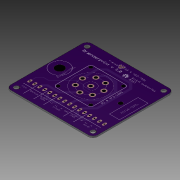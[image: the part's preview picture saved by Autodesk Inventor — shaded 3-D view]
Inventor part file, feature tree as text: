
AUTODESK INVENTOR PART (.ipt)
format: ipt  version: 2015 (Build 190159000, 159)  size: 491,008 bytes
history: native  units: mm
features: other x4, sketch x3, extrude x1
ambient origin geometry x8: Origin, YZ Plane, XZ Plane, XY Plane, X Axis, Y Axis, Z Axis, Center Point
bodies: Solid1 (feature_tree)
feature tree (8):
  extrude  "Extrusion1"  Depth=82.54mm
  other  "Decal1"
  other  "Decal2"
  sketch  "Sketch1"  dims[d0=88.57mm d2=82.54mm]
  sketch  "Sketch2"  dims[d3=78.0mm]
  other  "Image2"
  sketch  "Sketch3"  dims[d4=72.0mm d5=5.285mm d6=5.27mm d7=5.0mm d8=4.5mm d9=4.5mm d10=4.5mm d11=4.5mm d12=1.5mm d13=0.0mm]
  other  "Image3"
